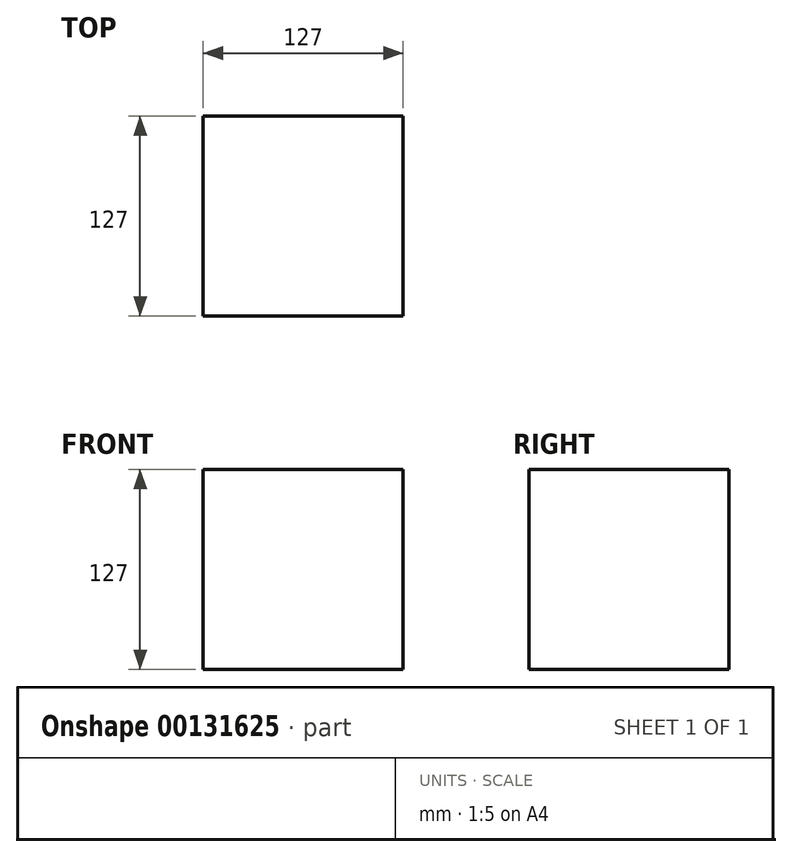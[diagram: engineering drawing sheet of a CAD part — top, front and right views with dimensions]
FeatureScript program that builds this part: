
annotation { "Feature Type Name" : "Feature", "Feature Type Description" : "" }
export const myFeature = defineFeature(function(context is Context, id is Id, definition is map)
    precondition{}
    {
        {
            var Q0;
            Q0=qCreatedBy(makeId("Front.planeOp"),FACE);
            var sketch = newSketch(context, id + "F0", { "sketchPlane" : qUnion([Q0])});
            skLineSegment(sketch, "E0.bottom", {"start": v(40.1, 59.62) * mm, "end": v(-86.9, 59.62) * mm});
            skLineSegment(sketch, "E0.top", {"start": v(40.1, -67.38) * mm, "end": v(-86.9, -67.38) * mm});
            skLineSegment(sketch, "E0.left", {"start": v(40.1, 59.62) * mm, "end": v(40.1, -67.38) * mm});
            skLineSegment(sketch, "E0.right", {"start": v(-86.9, 59.62) * mm, "end": v(-86.9, -67.38) * mm});
            skPoint(sketch, "E0.middle", {"position": v(-23.4, -3.88) * mm});
            skSolve(sketch);
        }
        {
            var Q0;
            Q0 = qSketchRegion(id + "F0", true);
            extrude(context, id + "F1", {"entities" : qUnion([Q0]), "depth" : 127 * mm});
        }
    });
